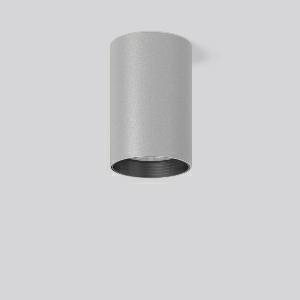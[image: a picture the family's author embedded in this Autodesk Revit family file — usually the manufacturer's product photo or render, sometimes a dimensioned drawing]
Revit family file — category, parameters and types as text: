
# Revit family: heledon_maxi_a_931235_004_da65
name_source: partatom
category: Lighting Fixtures
units: mm (PartAtom-declared; Revit-internal decimal feet)

## family parameters
Cut with Voids When Loaded = No
Host = Face
Light Source = No
Part Type = Normal
Room Calculation Point = No
Round Connector Dimension = Use Diameter
Shared = No

## types (1)
- HELEDON maxi A (1 x LED Modul 932 fresh meat, 1750 lm, 3200)
    Apparent Load = 33 VA
    Approval mark = CE
    CIE Flux Codes = 96 99 100 100 100
    Color Rendering = 90
    Color Temperature = 3200
    Default Elevation = 1800 mm
    Description = Series: HELEDON maxi
Cylindrical surface-mounted downlight. Housing: die-cast aluminium, powder-coated. Internal ceiling frame polycarbonate with bayonet mounting. Black plastic ring and recessed LED to prevent glare from the side. Optical assembly with lens made of plastic (polycarbonate) for the best homogeneous light distribution - can be changed without tools. Special LED for illumination of meat included. Suitable for Ceiling mounting. Easy installation with a separate ceiling frame with bayonet mounting and plug connection. Driver integrated. Connected via plug-in connector. High quality converter without flickering and stroboscopic effect. The following accessories can be mounted without use of tools: interchangeable lenses, decorative glasses, honeycomb louvre, clear and frosted diffusers, white interchangeable plastic ring. 
Colour: silver
Diameter: 123 mm
Height: 183 mm
Lamp: LED
Socket: without socket
Colour temperature: fresh meat
System power: 33 W
Rated luminous flux: 1750 lm
Luminous efficiency: 53 lm/W
Control gear: Regulated power supply
Protection class: I
Type of protection: IP 20
    Height = 183 mm
    Lamp = 1 x LED Modul 932 fresh meat
    Lamp Light Flux = 1750 lm
    Lamp count = 1
    Length = 123 mm
    Lifetime = 50000 h
    Luminous efficacy = 53 lm/W
    Manufacturer = RZB
    ModVariant = No
    Model = 931235.004
    Mounting Place = Ceiling
    Mounting Type = Surface mounted
    Number of Poles = 1
    OnlyDefault = Yes
    Power Factor = 1
    Product Name = HELEDON maxi A
    Product group = Surface mounted downlights
    ProductGroupID = 302
    Protection Class = Protection class I
    Protection Degree = IP 20
    RLX_Detail_Level = 1
    RLX_Emergency_Light_Flux = 0 lm
    RLX_Emergency_Type = 0
    RLX_Emergency_Type_DB = No
    RlxData = <blob elided: 97265 chars, md5=150cc68f>
    Socket = socket
    Standby Power = 0 W
    System Light Flux = 1750 lm
    System Power = 33 W
    Type Comments = Product without accessories
    Type Image = 931193.004.jpg
    URL = http://relux.com
    VarID = ---
    Voltage = 230 V
    Voltage Range = 220-240 V
    Weight = 0.00 kg
    Width = 0 mm  [stored 0 ft]

note: [stored X ft] marks values corroborated as IEEE doubles in the binary element streams (Revit-internal decimal feet)

## geometry (parser evidence)
native form markers: Blend x4, Sweep x11
no freeform markers — native parametric forms only
